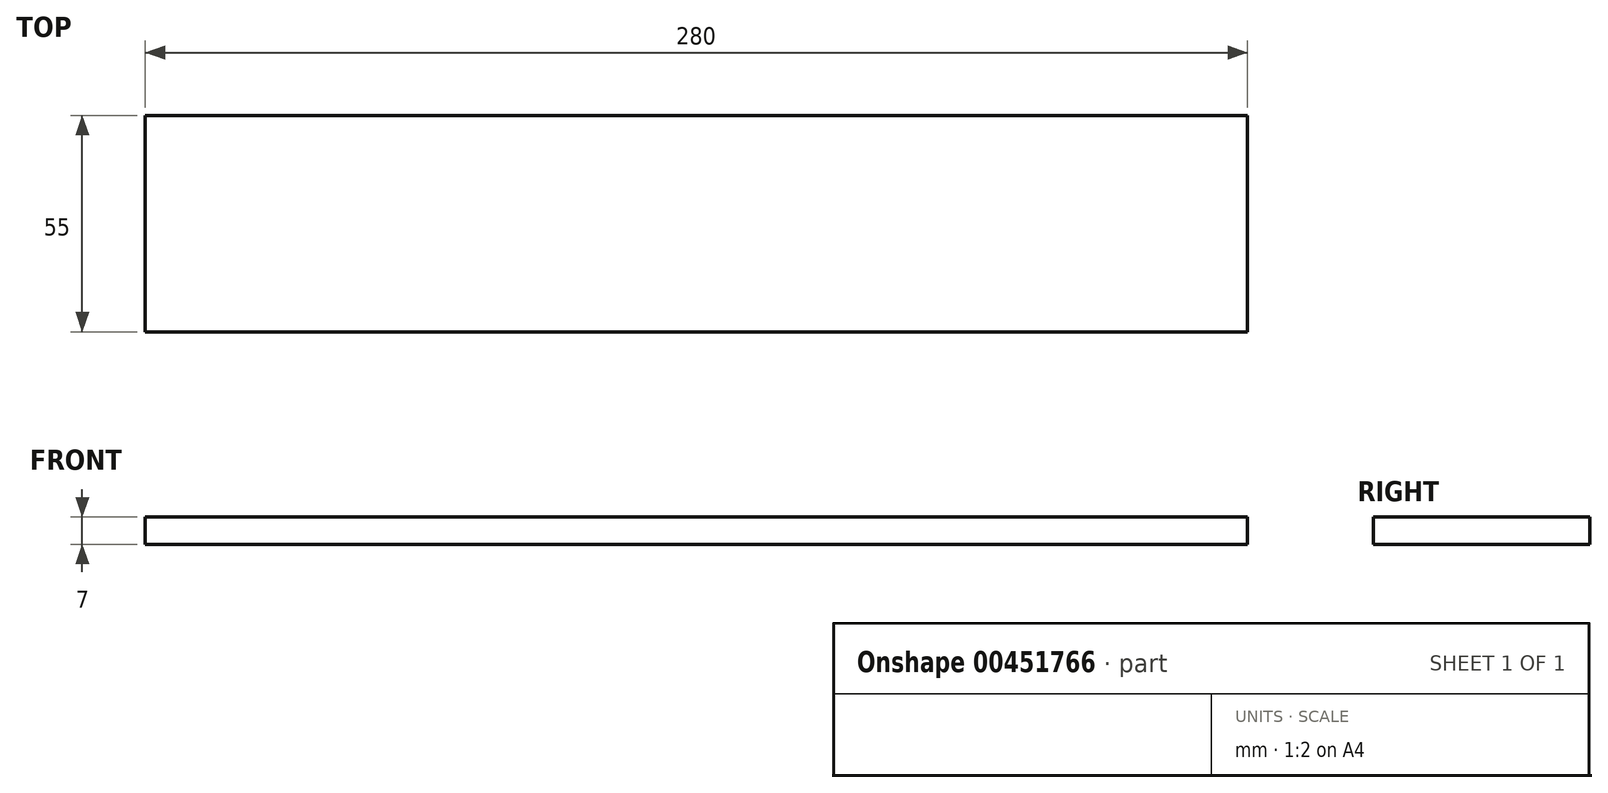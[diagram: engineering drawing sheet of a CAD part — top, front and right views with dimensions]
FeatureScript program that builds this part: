
annotation { "Feature Type Name" : "Feature", "Feature Type Description" : "" }
export const myFeature = defineFeature(function(context is Context, id is Id, definition is map)
    precondition{}
    {
        {
            var Q0;
            Q0=qCreatedBy(makeId("Top.planeOp"),FACE);
            var sketch = newSketch(context, id + "F0", { "sketchPlane" : qUnion([Q0])});
            skLineSegment(sketch, "E0.bottom", {"start": v(-140, 27.5) * mm, "end": v(140, 27.5) * mm});
            skLineSegment(sketch, "E0.top", {"start": v(-140, -27.5) * mm, "end": v(140, -27.5) * mm});
            skLineSegment(sketch, "E0.left", {"start": v(-140, 27.5) * mm, "end": v(-140, -27.5) * mm});
            skLineSegment(sketch, "E0.right", {"start": v(140, 27.5) * mm, "end": v(140, -27.5) * mm});
            skPoint(sketch, "E0.middle", {"position": v(0, 0) * mm});
            skSolve(sketch);
        }
        {
            var Q0;
            Q0 = qSketchRegion(id + "F0", true);
            extrude(context, id + "F1", {"entities" : qUnion([Q0]), "depth" : 7 * mm, "offsetDistance" : 25 * mm});
        }
    });
